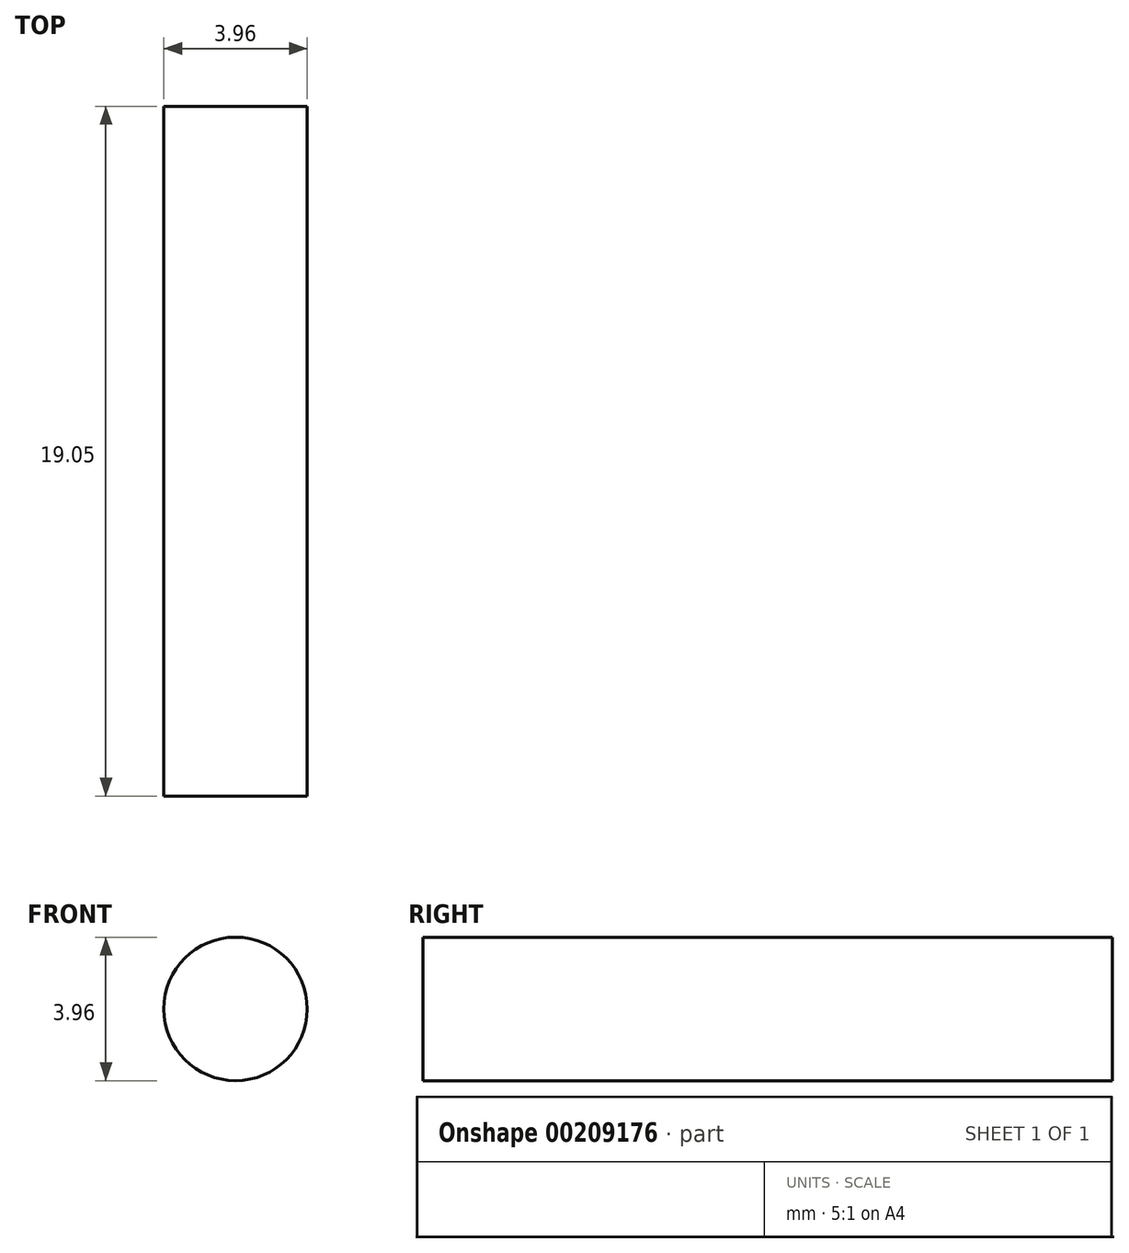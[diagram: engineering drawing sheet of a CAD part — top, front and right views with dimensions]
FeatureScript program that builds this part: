
annotation { "Feature Type Name" : "Feature", "Feature Type Description" : "" }
export const myFeature = defineFeature(function(context is Context, id is Id, definition is map)
    precondition{}
    {
        {
            var Q0;
            Q0=qCreatedBy(makeId("Front.planeOp"),FACE);
            var sketch = newSketch(context, id + "F0", { "sketchPlane" : qUnion([Q0])});
            skCircle(sketch, "E0", {"center": v(0, 0) * mm, "radius": 1.98 * mm});
            skSolve(sketch);
        }
        {
            var Q0;
            Q0 = qSketchRegion(id + "F0", true);
            extrude(context, id + "F1", {"entities" : qUnion([Q0]), "depth" : 19.05 * mm});
        }
    });
